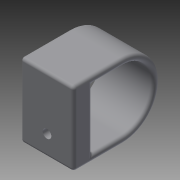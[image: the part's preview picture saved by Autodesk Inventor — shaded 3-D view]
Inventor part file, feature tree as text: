
AUTODESK INVENTOR PART (.ipt)
format: ipt  version: 2014 (Build 180170000, 170)  size: 206,848 bytes
history: native  units: mm
features: fillet x8, sketch x4, extrude x3, plane x2, hole x1
ambient origin geometry x8: Origin, YZ Plane, XZ Plane, XY Plane, X Axis, Y Axis, Z Axis, Center Point
bodies: Volumenkörper1 (feature_tree)
feature tree (18):
  extrude  "Extrusion1"  Depth=36.0mm
  extrude  "Extrusion2"  Depth=30.0mm
  fillet  "Rundung1"  Radius=30.0mm
  fillet  "Rundung2"  Radius=3.0mm
  fillet  "Rundung3"  Radius=3.0mm
  plane  "Arbeitsebene1"
  plane  "Arbeitsebene2"
  extrude  "Extrusion3"  Depth=15.0mm
  fillet  "Rundung4"  Radius=15.0mm
  hole  "Bohrung1"  [1 undecoded]
  fillet  "Rundung6"  [1 undecoded]
  fillet  "Rundung7"  Radius=20.0mm
  fillet  "Rundung8"  Radius=17.0mm
  fillet  "Rundung9"  Radius=3.0mm
  sketch  "Skizze1"  dims[d0=42.0mm d1=36.0mm]
  sketch  "Skizze2"  dims[d2=26.0mm d3=0.0mm d4=30.0mm d5=30.0mm d6=3.0mm d7=3.0mm]
  sketch  "Skizze3"  dims[d8=26.0mm d9=0.0mm d10=15.0mm d11=15.0mm]
  sketch  "Skizze4"  dims[d12=18.0mm d13=-3.0mm d14=-6.2mm d15=20.0mm d16=17.0mm d17=3.0mm d18=26.0mm d19=0.0mm d20=9.0mm d21=4.2mm d22=6.0mm d23=7.5mm d24=2.0mm d25=90.0deg d26=8.0mm d27=20.594885mm d29=13.0mm d31=10.0mm d32=1.5mm d33=1.5mm d34=1.5mm d35=1.5mm]
note: 2 required parameter values undecoded (feature->parameter linkage not recoverable at this tier; creation-order binding heuristic only, values carry confidence <= 0.55)
